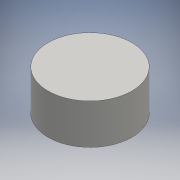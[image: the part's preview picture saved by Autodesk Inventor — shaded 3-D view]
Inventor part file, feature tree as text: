
AUTODESK INVENTOR PART (.ipt)
format: ipt  version: 2016 (Build 200138000, 138)  size: 92,672 bytes
history: native  units: mm
features: extrude x1, other x1, hole x1, sketch x1
ambient origin geometry x8: Origin, YZ Plane, XZ Plane, XY Plane, X Axis, Y Axis, Z Axis, Center Point
bodies: Solid1 (feature_tree)
feature tree (4):
  extrude  "Extrusion1"  Depth=17.5mm TaperAngle=0.0deg
  other  "Work Point1"
  hole  "Hole1"  [1 undecoded]
  sketch  "Sketch1"  dims[d0=36.5mm d1=17.5mm d2=0.0mm d3=10.0mm d4=10.0mm d5=35.5mm d6=6.0mm d7=4.0mm d8=2.0mm d9=90.0deg d10=15.5mm d11=0.0mm]
note: 1 required parameter value undecoded (feature->parameter linkage not recoverable at this tier; creation-order binding heuristic only, values carry confidence <= 0.55)
